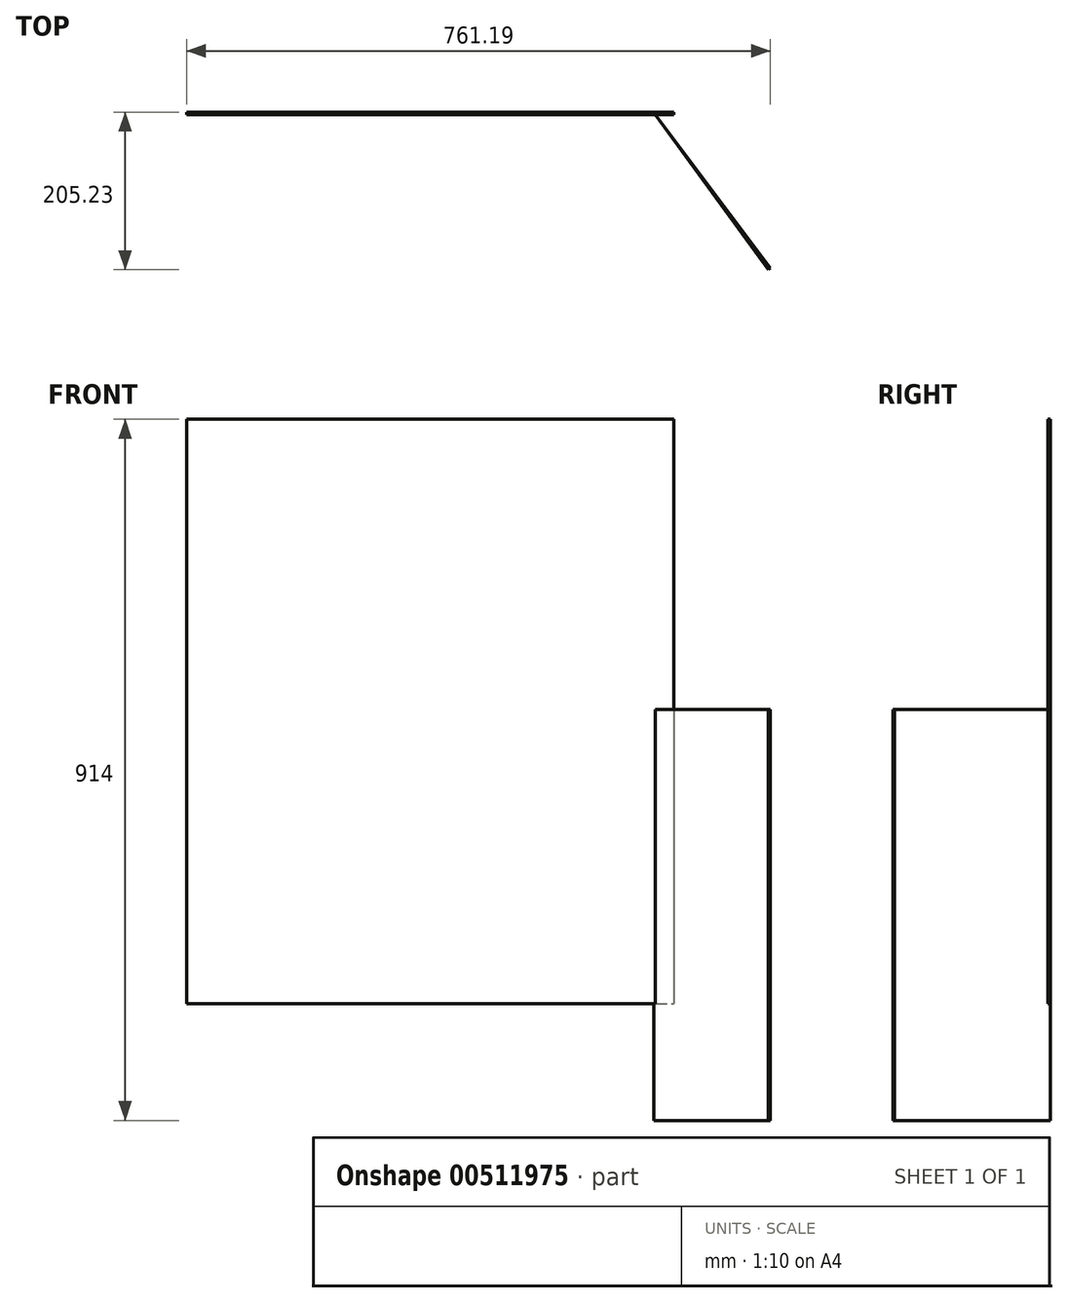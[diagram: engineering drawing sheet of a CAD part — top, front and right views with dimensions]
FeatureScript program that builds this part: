
annotation { "Feature Type Name" : "Feature", "Feature Type Description" : "" }
export const myFeature = defineFeature(function(context is Context, id is Id, definition is map)
    precondition{}
    {
        {
            var Q0;
            Q0=qCreatedBy(makeId("Front.planeOp"),FACE);
            var sketch = newSketch(context, id + "F0", { "sketchPlane" : qUnion([Q0])});
            skLineSegment(sketch, "E0.bottom", {"start": v(-761.2, 378.06) * mm, "end": v(-126.2, 378.06) * mm});
            skLineSegment(sketch, "E0.top", {"start": v(-761.2, -383.94) * mm, "end": v(-126.2, -383.94) * mm});
            skLineSegment(sketch, "E0.left", {"start": v(-761.2, 378.06) * mm, "end": v(-761.2, -383.94) * mm});
            skLineSegment(sketch, "E0.right", {"start": v(-126.2, 378.06) * mm, "end": v(-126.2, -383.94) * mm});
            skSolve(sketch);
        }
        {
            var Q0;
            Q0=makeQuery(id+"F0.imprint","IMPRINT",FACE,{"disambiguationData":[TD([[makeQuery(id+"F0.imprint","IMPRINT",EDGE,{"derivedFrom":sQuery(id+"F0.wireOp",EDGE,"E0.bottom")}),-1.0]])]});
            extrude(context, id + "F1", {"entities" : qUnion([Q0]), "depth" : 3.17 * mm});
        }
        {
            var Q0;
            Q0=qCreatedBy(makeId("Top.planeOp"),FACE);
            var sketch = newSketch(context, id + "F2", { "sketchPlane" : qUnion([Q0])});
            skLineSegment(sketch, "E1", {"start": v(-152.24, 0) * mm, "end": v(0, -203.32) * mm});
            skLineSegment(sketch, "E2", {"start": v(0, -203.32) * mm, "end": v(-2.54, -205.23) * mm});
            skLineSegment(sketch, "E3", {"start": v(-2.54, -205.23) * mm, "end": v(-152.24, -0.02) * mm});
            skLineSegment(sketch, "E4", {"start": v(-152.24, -0.02) * mm, "end": v(-152.24, 0) * mm});
            skSolve(sketch);
        }
        {
            var Q0;
            Q0=makeQuery(id+"F2.imprint","IMPRINT",FACE,{"disambiguationData":[TD([[makeQuery(id+"F2.imprint","IMPRINT",EDGE,{"derivedFrom":sQuery(id+"F2.wireOp",EDGE,"E1")}),-1.0]])]});
            extrude(context, id + "F3", {"entities" : qUnion([Q0]), "operationType" : NewBodyOperationType.ADD, "oppositeDirection" : true, "depth" : 535.94 * mm});
        }
    });
